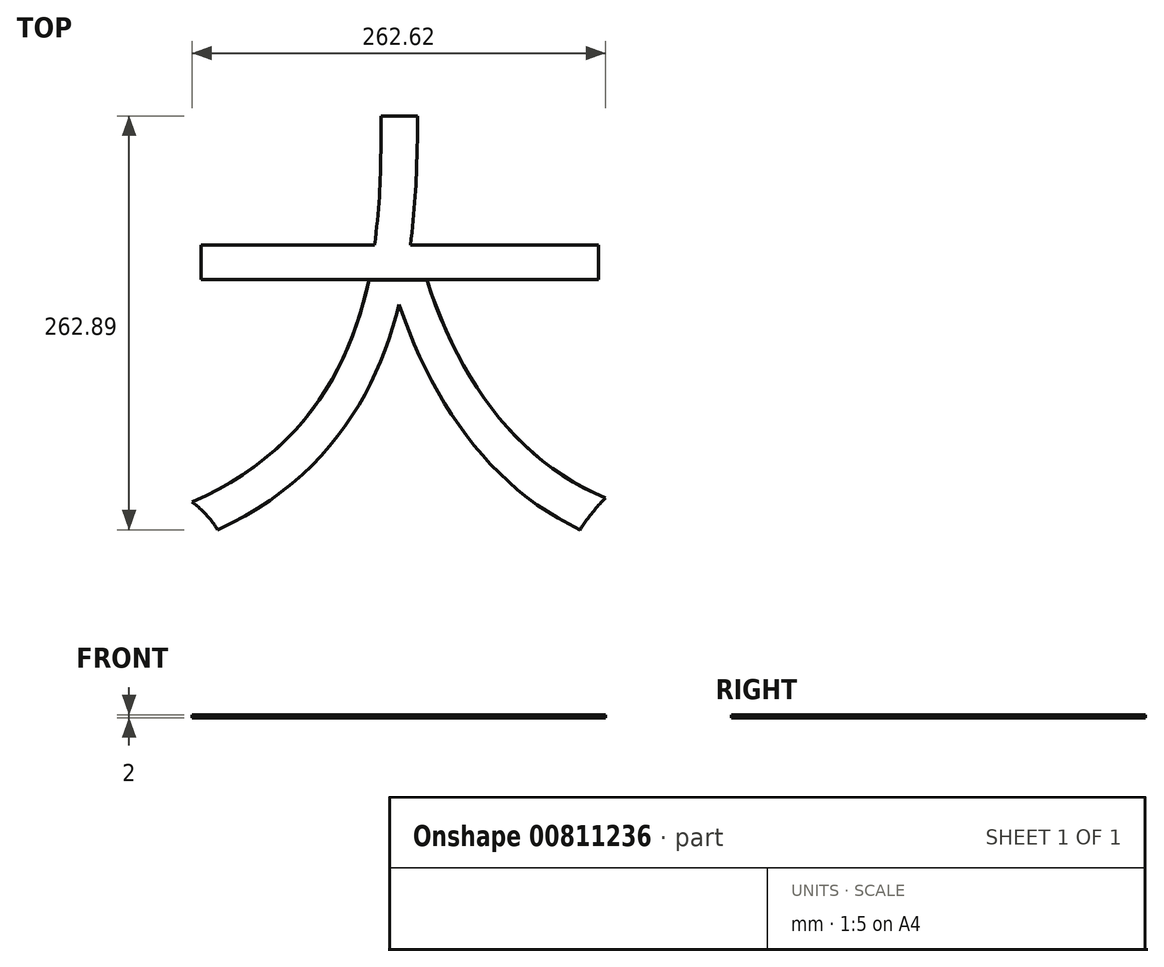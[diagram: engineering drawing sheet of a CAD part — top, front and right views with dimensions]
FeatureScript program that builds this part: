
annotation { "Feature Type Name" : "Feature", "Feature Type Description" : "" }
export const myFeature = defineFeature(function(context is Context, id is Id, definition is map)
    precondition{}
    {
        {
            var Q0;
            Q0=qCreatedBy(makeId("Top.planeOp"),FACE);
            var sketch = newSketch(context, id + "F0", { "sketchPlane" : qUnion([Q0])});
            skText(sketch, "E0", { "text": "大", "fontName": "NotoSansCJKtc-Regular.otf"});
            const initialGuessF0  = {"E0": [-0.00804, 0, 1, 0, 0.208]};
            skSetInitialGuess(sketch, initialGuessF0);
            skSolve(sketch);
        }
        {
            var Q0;
            Q0 = qSketchRegion(id + "F0", true);
            extrude(context, id + "F1", {"entities" : qUnion([Q0]), "depth" : 2 * mm, "offsetDistance" : 25.4 * mm});
        }
        {
            var Q0;
            Q0=makeQuery(id+"F1.opExtrude","CAP_FACE",FACE,{"disambiguationData":[OSD([sQuery(id+"F0.wireOp",EDGE,"E0.sketch_text.stroke-0"),sQuery(id+"F0.wireOp",EDGE,"E0.sketch_text.stroke-1"),sQuery(id+"F0.wireOp",EDGE,"E0.sketch_text.stroke-2"),sQuery(id+"F0.wireOp",EDGE,"E0.sketch_text.stroke-3"),sQuery(id+"F0.wireOp",EDGE,"E0.sketch_text.stroke-4"),sQuery(id+"F0.wireOp",EDGE,"E0.sketch_text.stroke-5"),sQuery(id+"F0.wireOp",EDGE,"E0.sketch_text.stroke-6"),sQuery(id+"F0.wireOp",EDGE,"E0.sketch_text.stroke-7"),sQuery(id+"F0.wireOp",EDGE,"E0.sketch_text.stroke-8"),sQuery(id+"F0.wireOp",EDGE,"E0.sketch_text.stroke-9"),sQuery(id+"F0.wireOp",EDGE,"E0.sketch_text.stroke-10"),sQuery(id+"F0.wireOp",EDGE,"E0.sketch_text.stroke-11"),sQuery(id+"F0.wireOp",EDGE,"E0.sketch_text.stroke-12"),sQuery(id+"F0.wireOp",EDGE,"E0.sketch_text.stroke-13"),sQuery(id+"F0.wireOp",EDGE,"E0.sketch_text.stroke-14")])],"isStart":false});
            var sketch = newSketch(context, id + "F2", { "sketchPlane" : qUnion([Q0])});
            skLineSegment(sketch, "E1", {"start": v(117.63, 137.22) * mm, "end": v(154.33, 137.22) * mm});
            skLineSegment(sketch, "E2", {"start": v(154.33, 137.22) * mm, "end": v(154.36, 137.12) * mm});
            skLineSegment(sketch, "E3", {"start": v(154.36, 137.12) * mm, "end": v(117.6, 137.12) * mm});
            skLineSegment(sketch, "E4", {"start": v(117.6, 137.12) * mm, "end": v(117.63, 137.22) * mm});
            skSolve(sketch);
        }
        {
            var Q0;
            Q0 = qSketchRegion(id + "F2", true);
            extrude(context, id + "F3", {"entities" : qUnion([Q0]), "operationType" : NewBodyOperationType.REMOVE, "oppositeDirection" : true, "depth" : 25.4 * mm, "offsetDistance" : 25.4 * mm});
        }
    });
